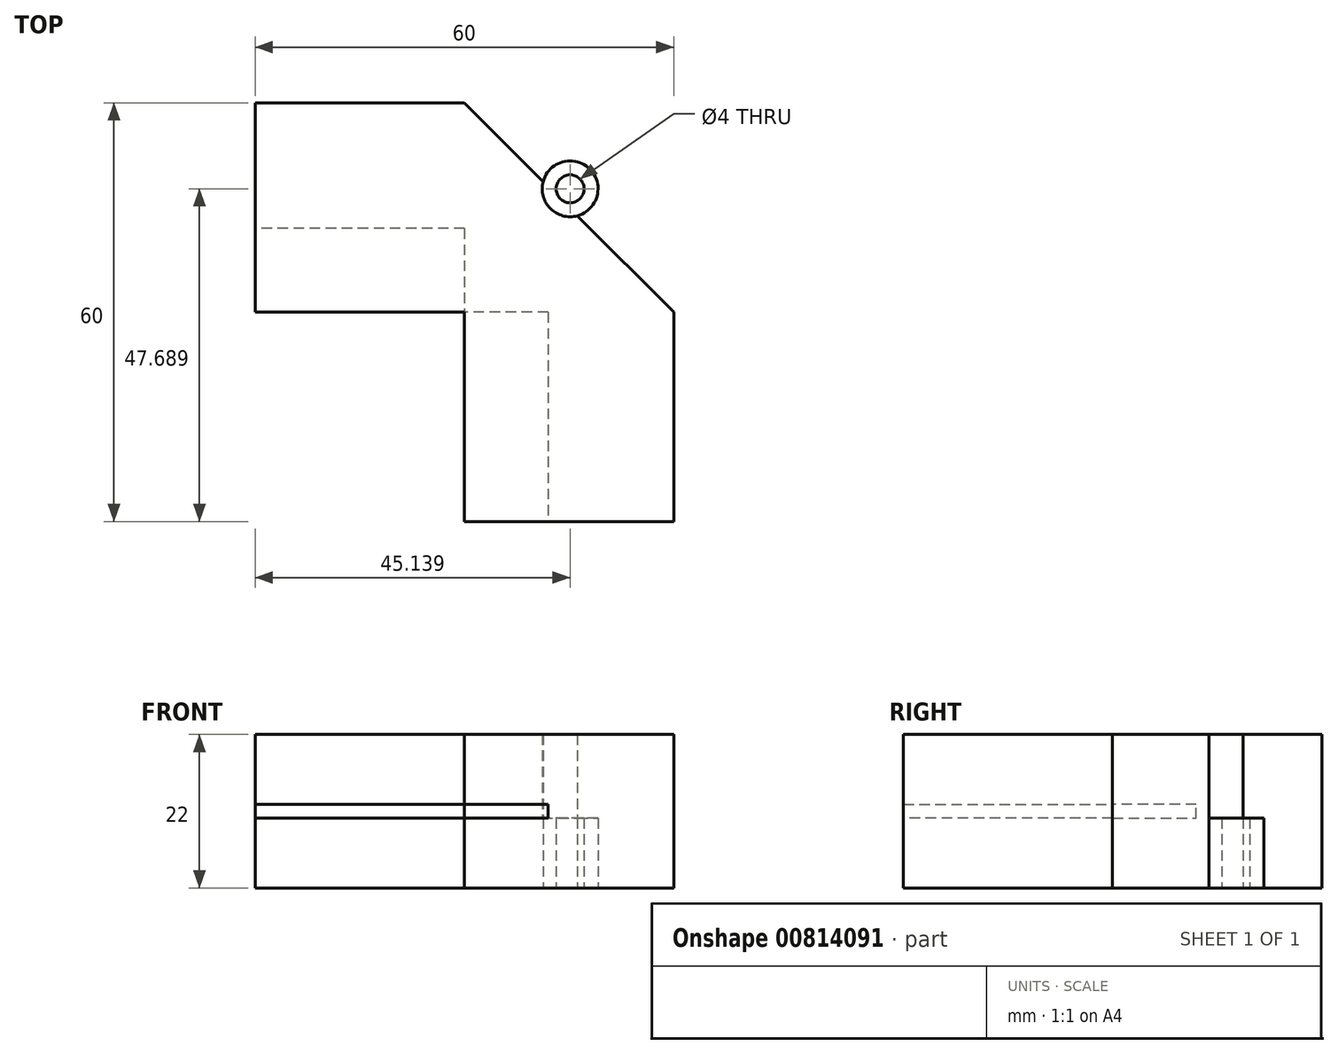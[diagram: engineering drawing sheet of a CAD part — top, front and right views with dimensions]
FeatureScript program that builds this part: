
annotation { "Feature Type Name" : "Feature", "Feature Type Description" : "" }
export const myFeature = defineFeature(function(context is Context, id is Id, definition is map)
    precondition{}
    {
        {
            var Q0;
            Q0=qCreatedBy(makeId("Top.planeOp"),FACE);
            var sketch = newSketch(context, id + "F0", { "sketchPlane" : qUnion([Q0])});
            skLineSegment(sketch, "E0.bottom", {"start": v(0, 0) * mm, "end": v(-30, 0) * mm});
            skLineSegment(sketch, "E0.top", {"start": v(0, 30) * mm, "end": v(-30, 30) * mm});
            skLineSegment(sketch, "E0.left", {"start": v(0, 0) * mm, "end": v(0, 30) * mm});
            skLineSegment(sketch, "E0.right", {"start": v(-30, 0) * mm, "end": v(-30, 30) * mm});
            skLineSegment(sketch, "E1.bottom", {"start": v(0, 0) * mm, "end": v(30, 0) * mm});
            skLineSegment(sketch, "E1.top", {"start": v(0, -30) * mm, "end": v(30, -30) * mm});
            skLineSegment(sketch, "E1.left", {"start": v(0, 0) * mm, "end": v(0, -30) * mm});
            skLineSegment(sketch, "E1.right", {"start": v(30, 0) * mm, "end": v(30, -30) * mm});
            skLineSegment(sketch, "E2", {"start": v(0, 30) * mm, "end": v(30, 0) * mm});
            skCircle(sketch, "E3", {"center": v(15.14, 17.69) * mm, "radius": 2 * mm});
            skCircle(sketch, "E4", {"center": v(15.14, 17.69) * mm, "radius": 4 * mm});
            skSolve(sketch);
        }
        {
            var Q0;
            Q0=makeQuery(id+"F0.imprint","IMPRINT",FACE,{"disambiguationData":[TD([[makeQuery(id+"F0.imprint","IMPRINT",EDGE,{"derivedFrom":sQuery(id+"F0.wireOp",EDGE,"E1.bottom")}),-1.0]])]});
            var Q1;
            Q1=makeQuery(id+"F0.imprint","IMPRINT",FACE,{"disambiguationData":[TD([[makeQuery(id+"F0.imprint","IMPRINT",EDGE,{"derivedFrom":sQuery(id+"F0.wireOp",EDGE,"E0.left")}),-1.0]])]});
            var Q2;
            Q2=makeQuery(id+"F0.imprint","IMPRINT",FACE,{"disambiguationData":[TD([[makeQuery(id+"F0.imprint","IMPRINT",EDGE,{"derivedFrom":sQuery(id+"F0.wireOp",EDGE,"E0.bottom")}),-1.0]])]});
            extrude(context, id + "F1", {"entities" : qUnion([Q0, Q1, Q2]), "depth" : 12 * mm, "offsetDistance" : 25 * mm});
        }
        {
            var Q0;
            Q0=makeQuery(id+"F1.opExtrude","CAP_FACE",FACE,{"disambiguationData":[OSD([sQuery(id+"F0.wireOp",EDGE,"E0.bottom"),sQuery(id+"F0.wireOp",EDGE,"E0.top"),sQuery(id+"F0.wireOp",EDGE,"E0.right"),sQuery(id+"F0.wireOp",EDGE,"E1.top"),sQuery(id+"F0.wireOp",EDGE,"E1.left"),sQuery(id+"F0.wireOp",EDGE,"E1.right"),sQuery(id+"F0.wireOp",EDGE,"E2")])],"isStart":false});
            var sketch = newSketch(context, id + "F2", { "sketchPlane" : qUnion([Q0])});
            skLineSegment(sketch, "E5.bottom", {"start": v(-30, 0) * mm, "end": v(16.32, 0) * mm});
            skLineSegment(sketch, "E5.top", {"start": v(-30, 12) * mm, "end": v(16.32, 12) * mm});
            skLineSegment(sketch, "E5.left", {"start": v(-30, 0) * mm, "end": v(-30, 12) * mm});
            skLineSegment(sketch, "E5.right", {"start": v(16.32, 0) * mm, "end": v(16.32, 12) * mm});
            skLineSegment(sketch, "E6.bottom", {"start": v(0, -30) * mm, "end": v(12, -30) * mm});
            skLineSegment(sketch, "E6.top", {"start": v(0, 12) * mm, "end": v(12, 12) * mm});
            skLineSegment(sketch, "E6.left", {"start": v(0, -30) * mm, "end": v(0, 12) * mm});
            skLineSegment(sketch, "E6.right", {"start": v(12, -30) * mm, "end": v(12, 12) * mm});
            skSolve(sketch);
        }
        {
            var Q0;
            {var subQ5=sQuery(id+"F2.wireOp",EDGE,"E6.bottom");Q0=makeQuery(id+"F2.imprint","IMPRINT",FACE,{"disambiguationData":[TD([[makeQuery(id+"F2.imprint","IMPRINT",EDGE,{"derivedFrom":subQ5}),1.0]])]});}
            var Q1;
            {var subQ5=sQuery(id+"F2.wireOp",EDGE,"E6.top");Q1=makeQuery(id+"F2.imprint","IMPRINT",FACE,{"disambiguationData":[TD([[makeQuery(id+"F2.imprint","IMPRINT",EDGE,{"derivedFrom":subQ5}),-1.0]])]});}
            var Q2;
            {var subQ3=sQuery(id+"F2.wireOp",EDGE,"E5.left");Q2=makeQuery(id+"F2.imprint","IMPRINT",FACE,{"disambiguationData":[TD([[makeQuery(id+"F2.imprint","IMPRINT",EDGE,{"derivedFrom":subQ3}),-1.0]])]});}
            extrude(context, id + "F3", {"entities" : qUnion([Q0, Q1, Q2]), "operationType" : NewBodyOperationType.REMOVE, "oppositeDirection" : true, "depth" : 3.5 * mm, "offsetDistance" : 25 * mm});
        }
        {
            var Q0;
            Q0=makeQuery(id+"F1.opExtrude","CAP_FACE",FACE,{"disambiguationData":[OSD([sQuery(id+"F0.wireOp",EDGE,"E0.bottom"),sQuery(id+"F0.wireOp",EDGE,"E0.top"),sQuery(id+"F0.wireOp",EDGE,"E0.right"),sQuery(id+"F0.wireOp",EDGE,"E1.top"),sQuery(id+"F0.wireOp",EDGE,"E1.left"),sQuery(id+"F0.wireOp",EDGE,"E1.right"),sQuery(id+"F0.wireOp",EDGE,"E2")])],"isStart":false});
            var sketch = newSketch(context, id + "F4", { "sketchPlane" : qUnion([Q0])});
            skLineSegment(sketch, "E7.bottom", {"start": v(-30, 30) * mm, "end": v(0, 30) * mm});
            skLineSegment(sketch, "E7.top", {"start": v(-30, 0) * mm, "end": v(0, 0) * mm});
            skLineSegment(sketch, "E7.left", {"start": v(-30, 30) * mm, "end": v(-30, 0) * mm});
            skLineSegment(sketch, "E7.right", {"start": v(0, 30) * mm, "end": v(0, 0) * mm});
            skLineSegment(sketch, "E8.bottom", {"start": v(0, 0) * mm, "end": v(30, 0) * mm});
            skLineSegment(sketch, "E8.top", {"start": v(0, -30) * mm, "end": v(30, -30) * mm});
            skLineSegment(sketch, "E8.left", {"start": v(0, 0) * mm, "end": v(0, -30) * mm});
            skLineSegment(sketch, "E8.right", {"start": v(30, 0) * mm, "end": v(30, -30) * mm});
            skLineSegment(sketch, "E9", {"start": v(0, 30) * mm, "end": v(11.74, 18.26) * mm});
            skSolve(sketch);
        }
        {
            var Q0;
            {var subQ0=sQuery(id+"F4.wireOp",EDGE,"E7.top");Q0=makeQuery(id+"F4.imprint","IMPRINT",FACE,{"disambiguationData":[TD([[makeQuery(id+"F4.imprint","IMPRINT",EDGE,{"derivedFrom":subQ0}),1.0]])]});}
            var Q1;
            {var subQ0=sQuery(id+"F4.wireOp",EDGE,"E8.left");Q1=makeQuery(id+"F4.imprint","IMPRINT",FACE,{"disambiguationData":[TD([[makeQuery(id+"F4.imprint","IMPRINT",EDGE,{"derivedFrom":subQ0}),1.0]])]});}
            var Q2;
            {var subQ3=sQuery(id+"F4.wireOp",EDGE,"E9");Q2=makeQuery(id+"F4.imprint","IMPRINT",FACE,{"disambiguationData":[TD([[makeQuery(id+"F4.imprint","IMPRINT",EDGE,{"derivedFrom":subQ3}),-1.0]])]});}
            var Q3;
            {var subQ0=sQuery(id+"F4.wireOp",EDGE,"E8.bottom");var subQ5=makeQuery(id+"F3.boolean.opBoolean","COPY",EDGE,{"derivedFrom":makeQuery(id+"F3.opExtrude","CAP_EDGE",EDGE,{"disambiguationData":[OSD([sQuery(id+"F2.wireOp",EDGE,"E6.right")])],"isStart":true})});var subQ7=makeQuery(id+"F4.imprint","INTERSECT",VERTEX,{"derivedFrom":[subQ5,subQ0]});Q3=makeQuery(id+"F4.imprint","IMPRINT",FACE,{"disambiguationData":[TD([[makeQuery(id+"F4.imprint","IMPRINT",EDGE,{"disambiguationData":[TD([[subQ7,-1.0]])],"derivedFrom":subQ5}),1.0]])]});}
            var Q4;
            {var subQ0=sQuery(id+"F4.wireOp",EDGE,"E7.bottom");Q4=makeQuery(id+"F4.imprint","IMPRINT",FACE,{"disambiguationData":[TD([[makeQuery(id+"F4.imprint","IMPRINT",EDGE,{"derivedFrom":subQ0}),1.0]])]});}
            var Q5;
            {var subQ0=sQuery(id+"F4.wireOp",EDGE,"E8.right");Q5=makeQuery(id+"F4.imprint","IMPRINT",FACE,{"disambiguationData":[TD([[makeQuery(id+"F4.imprint","IMPRINT",EDGE,{"derivedFrom":subQ0}),-1.0]])]});}
            extrude(context, id + "F5", {"entities" : qUnion([Q0, Q1, Q2, Q3, Q4, Q5]), "operationType" : NewBodyOperationType.ADD, "depth" : 10 * mm, "offsetDistance" : 25 * mm});
        }
        {
            var Q0;
            Q0 = qSketchRegion(id + "F0", true);
            extrude(context, id + "F6", {"entities" : qUnion([Q0]), "operationType" : NewBodyOperationType.ADD, "depth" : 10 * mm, "offsetDistance" : 25 * mm});
        }
    });
